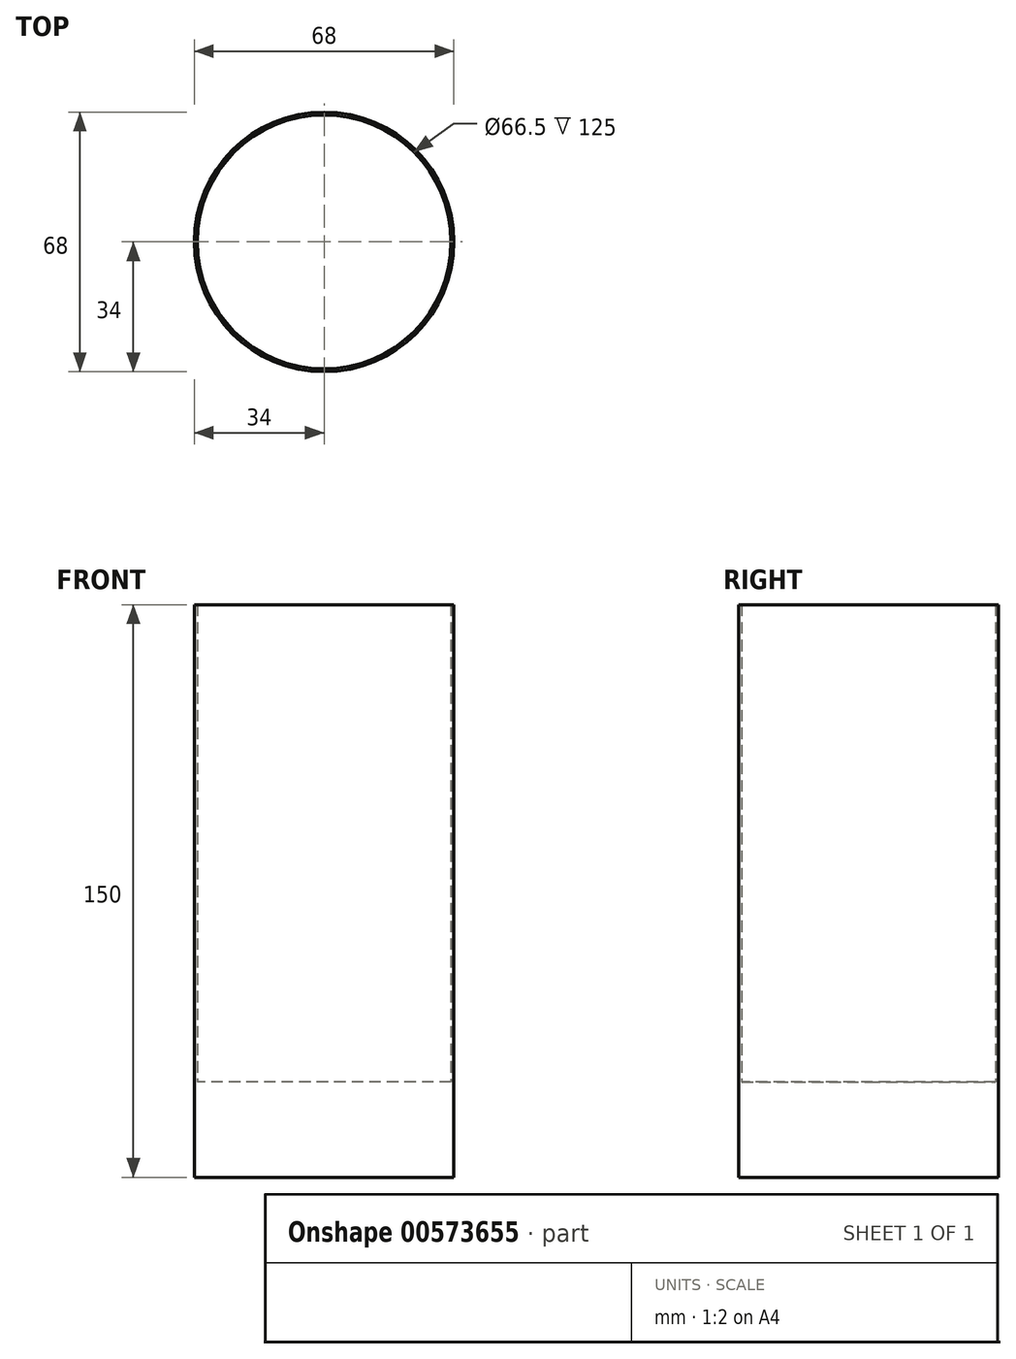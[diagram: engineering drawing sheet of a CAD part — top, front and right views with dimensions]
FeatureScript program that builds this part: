
annotation { "Feature Type Name" : "Feature", "Feature Type Description" : "" }
export const myFeature = defineFeature(function(context is Context, id is Id, definition is map)
    precondition{}
    {
        {
            var Q0;
            Q0=qCreatedBy(makeId("Top.planeOp"),FACE);
            var sketch = newSketch(context, id + "F0", { "sketchPlane" : qUnion([Q0])});
            skCircle(sketch, "E0", {"center": v(0, 0) * mm, "radius": 34 * mm});
            skCircle(sketch, "E1", {"center": v(0, 0) * mm, "radius": 33.25 * mm});
            skSolve(sketch);
        }
        {
            var Q0;
            Q0 = qSketchRegion(id + "F0", true);
            extrude(context, id + "F1", {"entities" : qUnion([Q0]), "depth" : 150 * mm, "offsetDistance" : 25 * mm});
        }
        {
            var Q0;
            Q0=qCreatedBy(makeId("Top.planeOp"),FACE);
            var sketch = newSketch(context, id + "F2", { "sketchPlane" : qUnion([Q0])});
            skCircle(sketch, "E2", {"center": v(0, 0) * mm, "radius": 33.33 * mm});
            skSolve(sketch);
        }
        {
            var Q0;
            Q0 = qSketchRegion(id + "F2", true);
            extrude(context, id + "F3", {"entities" : qUnion([Q0]), "operationType" : NewBodyOperationType.ADD, "depth" : 25 * mm, "offsetDistance" : 25 * mm});
        }
    });
